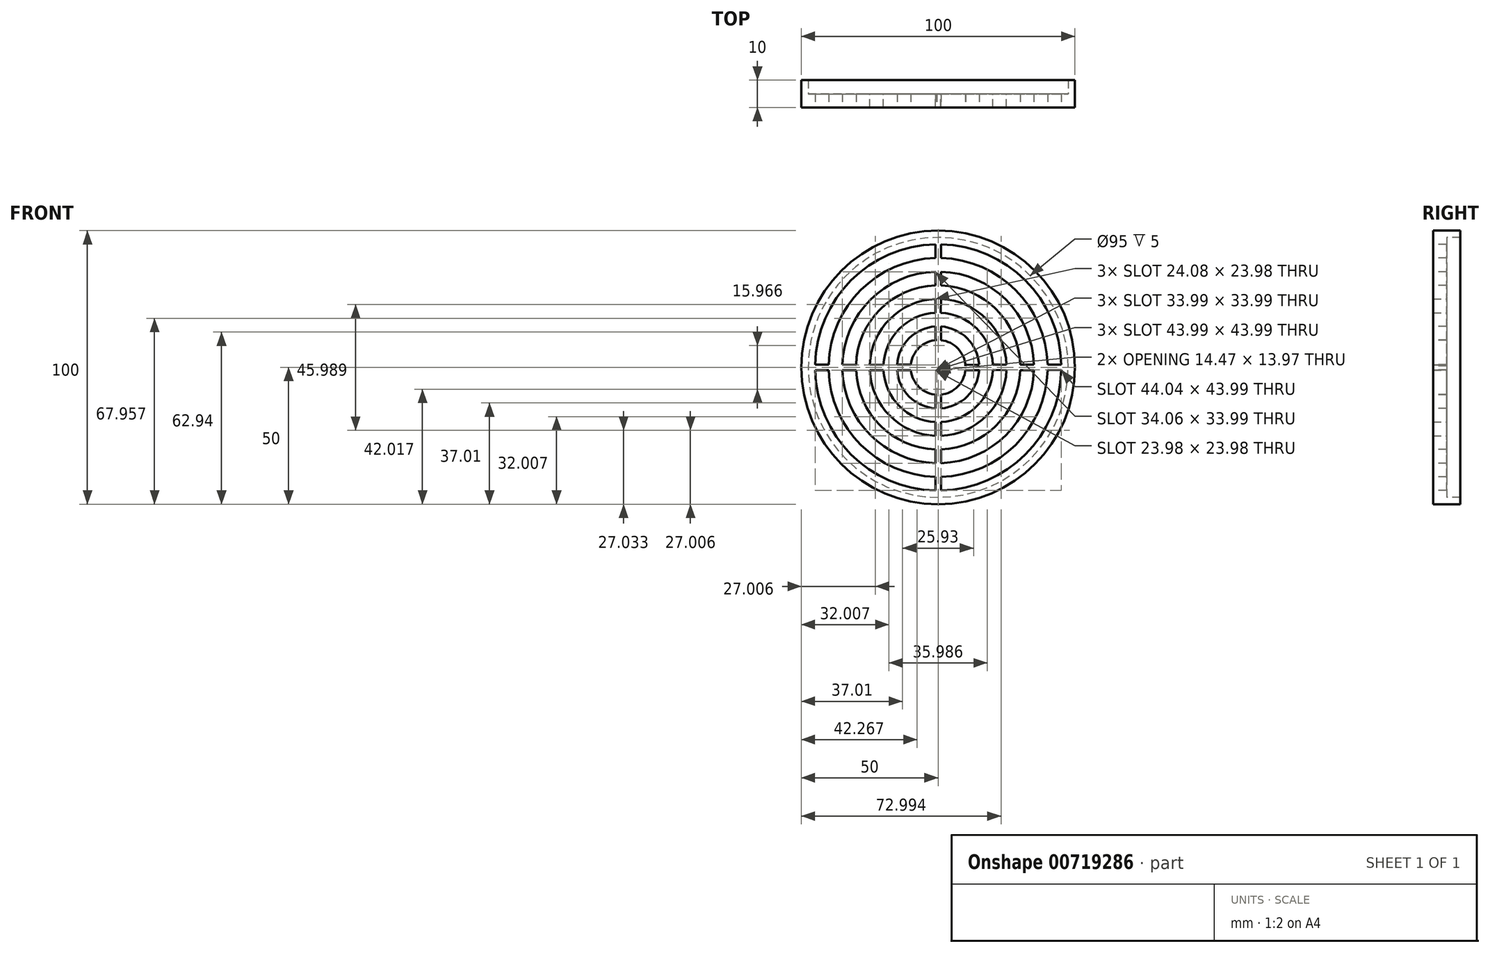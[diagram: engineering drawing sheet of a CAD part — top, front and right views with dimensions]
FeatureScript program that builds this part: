
annotation { "Feature Type Name" : "Feature", "Feature Type Description" : "" }
export const myFeature = defineFeature(function(context is Context, id is Id, definition is map)
    precondition{}
    {
        {
            var Q0;
            Q0=qCreatedBy(makeId("Front.planeOp"),FACE);
            var sketch = newSketch(context, id + "F0", { "sketchPlane" : qUnion([Q0])});
            skCircle(sketch, "E0", {"center": v(0, 0) * mm, "radius": 50 * mm});
            skSolve(sketch);
        }
        {
            var Q0;
            Q0=makeQuery(id+"F0.imprint","IMPRINT",FACE,{"disambiguationData":[TD([[makeQuery(id+"F0.imprint","IMPRINT",EDGE,{"derivedFrom":sQuery(id+"F0.wireOp",EDGE,"E0")}),1.0]])]});
            extrude(context, id + "F1", {"entities" : qUnion([Q0]), "depth" : 5 * mm, "offsetDistance" : 25 * mm});
        }
        {
            var Q0;
            Q0=makeQuery(id+"F1.opExtrude","CAP_FACE",FACE,{"disambiguationData":[OSD([sQuery(id+"F0.wireOp",EDGE,"E0")])],"isStart":false});
            var sketch = newSketch(context, id + "F2", { "sketchPlane" : qUnion([Q0])});
            skCircle(sketch, "E1", {"center": v(0, 0) * mm, "radius": 45 * mm});
            skCircle(sketch, "E2", {"center": v(0, 0) * mm, "radius": 40 * mm});
            skLineSegment(sketch, "E3", {"start": v(-1, 44.99) * mm, "end": v(-1, 39.99) * mm});
            skLineSegment(sketch, "E4", {"start": v(1, 44.99) * mm, "end": v(1, 39.99) * mm});
            skLineSegment(sketch, "E5", {"start": v(44.99, -1) * mm, "end": v(39.99, -0.94) * mm});
            skLineSegment(sketch, "E6", {"start": v(-44.99, -1) * mm, "end": v(-39.99, -1) * mm});
            skLineSegment(sketch, "E7", {"start": v(-44.99, 1) * mm, "end": v(-39.99, 1) * mm});
            skLineSegment(sketch, "E8", {"start": v(1, -44.99) * mm, "end": v(1, -39.99) * mm});
            skLineSegment(sketch, "E9", {"start": v(-1, -44.99) * mm, "end": v(-1, -39.99) * mm});
            skLineSegment(sketch, "E10", {"start": v(44.99, -1) * mm, "end": v(44.99, 1) * mm});
            skLineSegment(sketch, "E11", {"start": v(44.99, 1) * mm, "end": v(39.99, 1) * mm});
            skSolve(sketch);
        }
        {
            var Q0;
            {var subQ0=sQuery(id+"F2.wireOp",EDGE,"E4");Q0=makeQuery(id+"F2.imprint","IMPRINT",FACE,{"disambiguationData":[TD([[makeQuery(id+"F2.imprint","IMPRINT",EDGE,{"derivedFrom":subQ0}),1.0]])]});}
            var Q1;
            {var subQ0=sQuery(id+"F2.wireOp",EDGE,"E5");Q1=makeQuery(id+"F2.imprint","IMPRINT",FACE,{"disambiguationData":[TD([[makeQuery(id+"F2.imprint","IMPRINT",EDGE,{"derivedFrom":subQ0}),1.0]])]});}
            var Q2;
            {var subQ0=sQuery(id+"F2.wireOp",EDGE,"E3");Q2=makeQuery(id+"F2.imprint","IMPRINT",FACE,{"disambiguationData":[TD([[makeQuery(id+"F2.imprint","IMPRINT",EDGE,{"derivedFrom":subQ0}),-1.0]])]});}
            var Q3;
            {var subQ0=sQuery(id+"F2.wireOp",EDGE,"E6");Q3=makeQuery(id+"F2.imprint","IMPRINT",FACE,{"disambiguationData":[TD([[makeQuery(id+"F2.imprint","IMPRINT",EDGE,{"derivedFrom":subQ0}),-1.0]])]});}
            extrude(context, id + "F3", {"entities" : qUnion([Q0, Q1, Q2, Q3]), "operationType" : NewBodyOperationType.REMOVE, "oppositeDirection" : true, "depth" : 25 * mm, "offsetDistance" : 25 * mm});
        }
        {
            var Q0;
            Q0=makeQuery(id+"F1.opExtrude","CAP_FACE",FACE,{"disambiguationData":[OSD([sQuery(id+"F0.wireOp",EDGE,"E0")])],"isStart":false});
            var sketch = newSketch(context, id + "F4", { "sketchPlane" : qUnion([Q0])});
            skCircle(sketch, "E12", {"center": v(0, 0) * mm, "radius": 35 * mm});
            skCircle(sketch, "E13", {"center": v(0, 0) * mm, "radius": 30 * mm});
            skLineSegment(sketch, "E14", {"start": v(0, 30) * mm, "end": v(0, 35) * mm});
            skLineSegment(sketch, "E15", {"start": v(0, 35) * mm, "end": v(-1, 34.99) * mm});
            skLineSegment(sketch, "E16", {"start": v(-1, 34.99) * mm, "end": v(-1, 29.98) * mm});
            skLineSegment(sketch, "E17", {"start": v(-1, 29.98) * mm, "end": v(1, 29.98) * mm});
            skLineSegment(sketch, "E18", {"start": v(1, 29.98) * mm, "end": v(1, 35) * mm});
            skLineSegment(sketch, "E19", {"start": v(30, 0) * mm, "end": v(35, 0) * mm});
            skLineSegment(sketch, "E20", {"start": v(35, 0) * mm, "end": v(35, 1) * mm});
            skLineSegment(sketch, "E21", {"start": v(35, 1) * mm, "end": v(29.98, 1) * mm});
            skLineSegment(sketch, "E22", {"start": v(35, 0) * mm, "end": v(34.99, -1) * mm});
            skLineSegment(sketch, "E23", {"start": v(34.99, -1) * mm, "end": v(29.98, -1) * mm});
            skLineSegment(sketch, "E24", {"start": v(0, -30) * mm, "end": v(0, -35) * mm});
            skLineSegment(sketch, "E25", {"start": v(0, -35) * mm, "end": v(-1, -34.99) * mm});
            skLineSegment(sketch, "E26", {"start": v(-1, -34.99) * mm, "end": v(-1, -29.98) * mm});
            skLineSegment(sketch, "E27", {"start": v(-1, -29.98) * mm, "end": v(1, -29.98) * mm});
            skLineSegment(sketch, "E28", {"start": v(1, -29.98) * mm, "end": v(1, -35) * mm});
            skLineSegment(sketch, "E29", {"start": v(-30, 0) * mm, "end": v(-35, 0) * mm});
            skLineSegment(sketch, "E30", {"start": v(-35, 0) * mm, "end": v(-34.99, 1) * mm});
            skLineSegment(sketch, "E31", {"start": v(-34.99, 1) * mm, "end": v(-29.99, 0.93) * mm});
            skLineSegment(sketch, "E32", {"start": v(-35, 0) * mm, "end": v(-34.99, -1) * mm});
            skLineSegment(sketch, "E33", {"start": v(-34.99, -1) * mm, "end": v(-29.98, -1) * mm});
            skSolve(sketch);
        }
        {
            var Q0;
            {var subQ0=sQuery(id+"F4.wireOp",EDGE,"E16");Q0=makeQuery(id+"F4.imprint","IMPRINT",FACE,{"disambiguationData":[TD([[makeQuery(id+"F4.imprint","IMPRINT",EDGE,{"derivedFrom":subQ0}),-1.0]])]});}
            var Q1;
            {var subQ0=sQuery(id+"F4.wireOp",EDGE,"E26");Q1=makeQuery(id+"F4.imprint","IMPRINT",FACE,{"disambiguationData":[TD([[makeQuery(id+"F4.imprint","IMPRINT",EDGE,{"derivedFrom":subQ0}),1.0]])]});}
            var Q2;
            {var subQ0=sQuery(id+"F4.wireOp",EDGE,"E23");Q2=makeQuery(id+"F4.imprint","IMPRINT",FACE,{"disambiguationData":[TD([[makeQuery(id+"F4.imprint","IMPRINT",EDGE,{"derivedFrom":subQ0}),1.0]])]});}
            var Q3;
            {var subQ0=sQuery(id+"F4.wireOp",EDGE,"E18");var subQ1=sQuery(id+"F4.wireOp",EDGE,"E12");var subQ2=makeQuery(id+"F4.imprint","INTERSECT",VERTEX,{"derivedFrom":[subQ1,subQ0]});Q3=makeQuery(id+"F4.imprint","IMPRINT",FACE,{"disambiguationData":[TD([[makeQuery(id+"F4.imprint","IMPRINT",EDGE,{"disambiguationData":[TD([[subQ2,1.0]])],"derivedFrom":subQ1}),1.0]])]});}
            extrude(context, id + "F5", {"entities" : qUnion([Q0, Q1, Q2, Q3]), "operationType" : NewBodyOperationType.REMOVE, "oppositeDirection" : true, "depth" : 25 * mm, "offsetDistance" : 25 * mm});
        }
        {
            var Q0;
            Q0=makeQuery(id+"F1.opExtrude","CAP_FACE",FACE,{"disambiguationData":[OSD([sQuery(id+"F0.wireOp",EDGE,"E0")])],"isStart":true});
            var sketch = newSketch(context, id + "F6", { "sketchPlane" : qUnion([Q0])});
            skCircle(sketch, "E34", {"center": v(0, 0) * mm, "radius": 25 * mm});
            skCircle(sketch, "E35", {"center": v(0, 0) * mm, "radius": 20 * mm});
            skLineSegment(sketch, "E36", {"start": v(0, -20) * mm, "end": v(0, -25) * mm});
            skLineSegment(sketch, "E37", {"start": v(0, -25) * mm, "end": v(1, -24.98) * mm});
            skLineSegment(sketch, "E38", {"start": v(1, -24.98) * mm, "end": v(1, -19.97) * mm});
            skLineSegment(sketch, "E39", {"start": v(0, -25) * mm, "end": v(-1, -24.98) * mm});
            skLineSegment(sketch, "E40", {"start": v(-1, -24.98) * mm, "end": v(-1, -19.97) * mm});
            skLineSegment(sketch, "E41", {"start": v(20, 0) * mm, "end": v(25, 0) * mm});
            skLineSegment(sketch, "E42", {"start": v(25, 0) * mm, "end": v(24.98, -1) * mm});
            skLineSegment(sketch, "E43", {"start": v(24.98, -1) * mm, "end": v(19.97, -1) * mm});
            skLineSegment(sketch, "E44", {"start": v(25, 0) * mm, "end": v(24.98, 1) * mm});
            skLineSegment(sketch, "E45", {"start": v(24.98, 1) * mm, "end": v(19.98, 0.9) * mm});
            skLineSegment(sketch, "E46", {"start": v(-20, 0) * mm, "end": v(-25, 0) * mm});
            skLineSegment(sketch, "E47", {"start": v(-25, 0) * mm, "end": v(-24.98, -1) * mm});
            skLineSegment(sketch, "E48", {"start": v(-24.98, -1) * mm, "end": v(-19.98, -0.9) * mm});
            skLineSegment(sketch, "E49", {"start": v(-25, 0) * mm, "end": v(-24.98, 1) * mm});
            skLineSegment(sketch, "E50", {"start": v(-24.98, 1) * mm, "end": v(-19.97, 1) * mm});
            skLineSegment(sketch, "E51", {"start": v(0, 25) * mm, "end": v(1, 24.98) * mm});
            skLineSegment(sketch, "E52", {"start": v(0, 25) * mm, "end": v(-1, 24.98) * mm});
            skLineSegment(sketch, "E53", {"start": v(-1, 24.98) * mm, "end": v(-0.9, 19.98) * mm});
            skLineSegment(sketch, "E54", {"start": v(1, 24.98) * mm, "end": v(1, 19.97) * mm});
            skSolve(sketch);
        }
        {
            var Q0;
            {var subQ0=sQuery(id+"F6.wireOp",EDGE,"E45");Q0=makeQuery(id+"F6.imprint","IMPRINT",FACE,{"disambiguationData":[TD([[makeQuery(id+"F6.imprint","IMPRINT",EDGE,{"derivedFrom":subQ0}),-1.0]])]});}
            var Q1;
            {var subQ0=sQuery(id+"F6.wireOp",EDGE,"E38");Q1=makeQuery(id+"F6.imprint","IMPRINT",FACE,{"disambiguationData":[TD([[makeQuery(id+"F6.imprint","IMPRINT",EDGE,{"derivedFrom":subQ0}),-1.0]])]});}
            var Q2;
            {var subQ0=sQuery(id+"F6.wireOp",EDGE,"E40");Q2=makeQuery(id+"F6.imprint","IMPRINT",FACE,{"disambiguationData":[TD([[makeQuery(id+"F6.imprint","IMPRINT",EDGE,{"derivedFrom":subQ0}),1.0]])]});}
            var Q3;
            {var subQ0=sQuery(id+"F6.wireOp",EDGE,"E50");Q3=makeQuery(id+"F6.imprint","IMPRINT",FACE,{"disambiguationData":[TD([[makeQuery(id+"F6.imprint","IMPRINT",EDGE,{"derivedFrom":subQ0}),1.0]])]});}
            extrude(context, id + "F7", {"entities" : qUnion([Q0, Q1, Q2, Q3]), "operationType" : NewBodyOperationType.REMOVE, "oppositeDirection" : true, "depth" : 25 * mm, "offsetDistance" : 25 * mm});
        }
        {
            var Q0;
            Q0=makeQuery(id+"F1.opExtrude","CAP_FACE",FACE,{"disambiguationData":[OSD([sQuery(id+"F0.wireOp",EDGE,"E0")])],"isStart":false});
            var sketch = newSketch(context, id + "F8", { "sketchPlane" : qUnion([Q0])});
            skCircle(sketch, "E55", {"center": v(0, 0) * mm, "radius": 15 * mm});
            skCircle(sketch, "E56", {"center": v(0, 0) * mm, "radius": 10 * mm});
            skLineSegment(sketch, "E57", {"start": v(0, 10) * mm, "end": v(0, 15) * mm});
            skLineSegment(sketch, "E58", {"start": v(10, 0) * mm, "end": v(15, 0) * mm});
            skLineSegment(sketch, "E59", {"start": v(-10, 0) * mm, "end": v(-15, 0) * mm});
            skLineSegment(sketch, "E60", {"start": v(0, -10) * mm, "end": v(0, -15) * mm});
            skLineSegment(sketch, "E61", {"start": v(0, 15) * mm, "end": v(1, 14.97) * mm});
            skLineSegment(sketch, "E62", {"start": v(0, 15) * mm, "end": v(-1, 14.97) * mm});
            skLineSegment(sketch, "E63", {"start": v(-1, 14.97) * mm, "end": v(-1, 10) * mm});
            skLineSegment(sketch, "E64", {"start": v(1, 14.97) * mm, "end": v(1, 9.95) * mm});
            skLineSegment(sketch, "E65", {"start": v(-15, 0) * mm, "end": v(-14.97, 1) * mm});
            skLineSegment(sketch, "E66", {"start": v(-14.97, 1) * mm, "end": v(-9.95, 1) * mm});
            skLineSegment(sketch, "E67", {"start": v(-15, 0) * mm, "end": v(-14.97, -1) * mm});
            skLineSegment(sketch, "E68", {"start": v(-14.97, -1) * mm, "end": v(-9.95, -1) * mm});
            skLineSegment(sketch, "E69", {"start": v(15, 0) * mm, "end": v(14.97, 1) * mm});
            skLineSegment(sketch, "E70", {"start": v(14.97, 1) * mm, "end": v(10, 0.83) * mm});
            skLineSegment(sketch, "E71", {"start": v(15, 0) * mm, "end": v(14.97, -1) * mm});
            skLineSegment(sketch, "E72", {"start": v(14.97, -1) * mm, "end": v(9.95, -1) * mm});
            skLineSegment(sketch, "E73", {"start": v(0, -15) * mm, "end": v(-1, -14.97) * mm});
            skLineSegment(sketch, "E74", {"start": v(-1, -14.97) * mm, "end": v(-1, -10) * mm});
            skLineSegment(sketch, "E75", {"start": v(0, -15) * mm, "end": v(1, -14.97) * mm});
            skLineSegment(sketch, "E76", {"start": v(1, -14.97) * mm, "end": v(1, -9.95) * mm});
            skLineSegment(sketch, "E77", {"start": v(-1, 10) * mm, "end": v(1, 9.95) * mm});
            skLineSegment(sketch, "E78", {"start": v(9.95, -1) * mm, "end": v(10, 0.83) * mm});
            skLineSegment(sketch, "E79", {"start": v(-9.95, -1) * mm, "end": v(-9.95, 1) * mm});
            skLineSegment(sketch, "E80", {"start": v(-1, -10) * mm, "end": v(1, -9.95) * mm});
            skSolve(sketch);
        }
        {
            var Q0;
            {var subQ2=sQuery(id+"F8.wireOp",EDGE,"E63");Q0=makeQuery(id+"F8.imprint","IMPRINT",FACE,{"disambiguationData":[TD([[makeQuery(id+"F8.imprint","IMPRINT",EDGE,{"derivedFrom":subQ2}),-1.0]])]});}
            var Q1;
            {var subQ1=sQuery(id+"F8.wireOp",EDGE,"E64");Q1=makeQuery(id+"F8.imprint","IMPRINT",FACE,{"disambiguationData":[TD([[makeQuery(id+"F8.imprint","IMPRINT",EDGE,{"derivedFrom":subQ1}),1.0]])]});}
            var Q2;
            {var subQ0=sQuery(id+"F8.wireOp",EDGE,"E72");Q2=makeQuery(id+"F8.imprint","IMPRINT",FACE,{"disambiguationData":[TD([[makeQuery(id+"F8.imprint","IMPRINT",EDGE,{"derivedFrom":subQ0}),1.0]])]});}
            var Q3;
            {var subQ1=sQuery(id+"F8.wireOp",EDGE,"E68");Q3=makeQuery(id+"F8.imprint","IMPRINT",FACE,{"disambiguationData":[TD([[makeQuery(id+"F8.imprint","IMPRINT",EDGE,{"derivedFrom":subQ1}),-1.0]])]});}
            extrude(context, id + "F9", {"entities" : qUnion([Q0, Q1, Q2, Q3]), "operationType" : NewBodyOperationType.REMOVE, "oppositeDirection" : true, "depth" : 25 * mm, "offsetDistance" : 25 * mm});
        }
        {
            var Q0;
            Q0=makeQuery(id+"F1.opExtrude","CAP_FACE",FACE,{"disambiguationData":[OSD([sQuery(id+"F0.wireOp",EDGE,"E0")])],"isStart":true});
            var sketch = newSketch(context, id + "F10", { "sketchPlane" : qUnion([Q0])});
            skCircle(sketch, "E81", {"center": v(0, 0) * mm, "radius": 47.5 * mm});
            skSolve(sketch);
        }
        {
            var Q0;
            Q0=makeQuery(id+"F10.imprint","IMPRINT",FACE,{"disambiguationData":[TD([[makeQuery(id+"F10.imprint","IMPRINT",EDGE,{"derivedFrom":sQuery(id+"F10.wireOp",EDGE,"E81")}),-1.0]])]});
            extrude(context, id + "F11", {"entities" : qUnion([Q0]), "operationType" : NewBodyOperationType.ADD, "depth" : 5 * mm, "offsetDistance" : 25 * mm});
        }
    });
